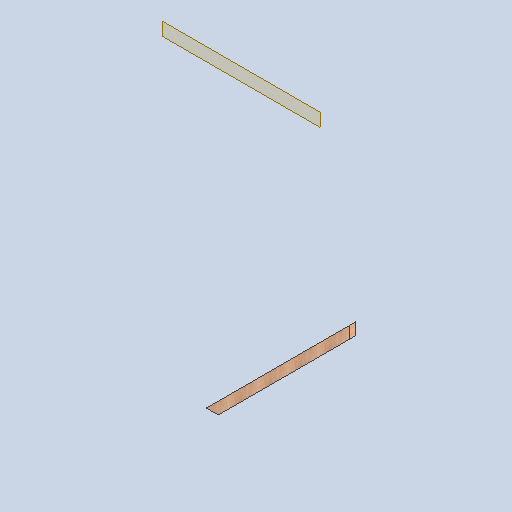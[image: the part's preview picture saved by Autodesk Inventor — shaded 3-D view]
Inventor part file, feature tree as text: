
AUTODESK INVENTOR PART (.ipt)
format: ipt  version: 2025 (Build 290162000, 162)  size: 88,576 bytes
history: native  units: in
note: dims shown in document units (in); Inventor stores cm internally (conversion verified against a paired STEP export)
features: other x3, sketch x1, plane x1
ambient origin geometry x8: Origin, YZ Plane, XZ Plane, XY Plane, X Axis, Y Axis, Z Axis, Center Point
bodies: Solid1 (feature_tree)
feature tree (5):
  other  "Leg slant.2.ipt"
  other  "Solid1::Leg slant.2.ipt"
  other  "TaggingFeature1"
  sketch  "Sketch1"  dims[d0=0.3937in]
  plane  "Work Plane1"
